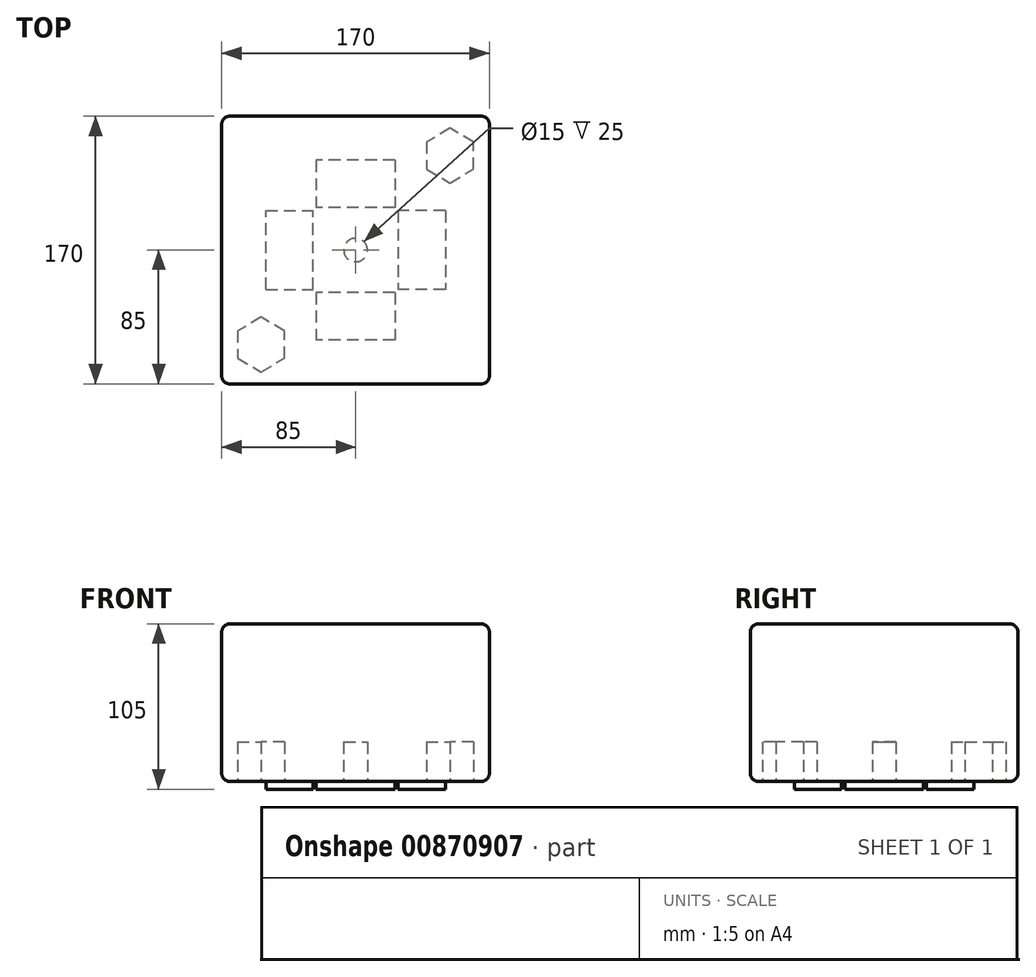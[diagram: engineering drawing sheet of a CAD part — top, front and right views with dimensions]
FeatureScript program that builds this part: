
annotation { "Feature Type Name" : "Feature", "Feature Type Description" : "" }
export const myFeature = defineFeature(function(context is Context, id is Id, definition is map)
    precondition{}
    {
        {
            var Q0;
            Q0=qCreatedBy(makeId("Top.planeOp"),FACE);
            var sketch = newSketch(context, id + "F0", { "sketchPlane" : qUnion([Q0])});
            skLineSegment(sketch, "E0.bottom", {"start": v(-85, 85) * mm, "end": v(85, 85) * mm});
            skLineSegment(sketch, "E0.top", {"start": v(-85, -85) * mm, "end": v(85, -85) * mm});
            skLineSegment(sketch, "E0.left", {"start": v(-85, 85) * mm, "end": v(-85, -85) * mm});
            skLineSegment(sketch, "E0.right", {"start": v(85, 85) * mm, "end": v(85, -85) * mm});
            skPoint(sketch, "E0.middle", {"position": v(0, 0) * mm});
            skSolve(sketch);
        }
        {
            var Q0;
            Q0=makeQuery(id+"F0.imprint","IMPRINT",FACE,{"disambiguationData":[TD([[makeQuery(id+"F0.imprint","IMPRINT",EDGE,{"derivedFrom":sQuery(id+"F0.wireOp",EDGE,"E0.bottom")}),-1.0]])]});
            extrude(context, id + "F1", {"entities" : qUnion([Q0]), "depth" : 100 * mm, "offsetDistance" : 25 * mm});
        }
        {
            var Q0;
            Q0=makeQuery(id+"F1.opExtrude","CAP_FACE",FACE,{"disambiguationData":[OSD([sQuery(id+"F0.wireOp",EDGE,"E0.bottom"),sQuery(id+"F0.wireOp",EDGE,"E0.top"),sQuery(id+"F0.wireOp",EDGE,"E0.left"),sQuery(id+"F0.wireOp",EDGE,"E0.right")])],"isStart":true});
            var sketch = newSketch(context, id + "F2", { "sketchPlane" : qUnion([Q0])});
            skCircle(sketch, "E1", {"center": v(0, 0) * mm, "radius": 7.5 * mm});
            skCircle(sketch, "E2.cCircle", {"center": v(-60, 60) * mm, "radius": 15 * mm, "construction": true});
            skLineSegment(sketch, "E2.0", {"start": v(-75, 68.66) * mm, "end": v(-60, 77.32) * mm});
            skLineSegment(sketch, "E2.1", {"start": v(-60, 77.32) * mm, "end": v(-45, 68.66) * mm});
            skLineSegment(sketch, "E2.2", {"start": v(-45, 68.66) * mm, "end": v(-45, 51.34) * mm});
            skLineSegment(sketch, "E2.3", {"start": v(-45, 51.34) * mm, "end": v(-60, 42.68) * mm});
            skLineSegment(sketch, "E2.4", {"start": v(-60, 42.68) * mm, "end": v(-75, 51.34) * mm});
            skLineSegment(sketch, "E2.5", {"start": v(-75, 51.34) * mm, "end": v(-75, 68.66) * mm});
            skPoint(sketch, "E2.0.midPoint", {"position": v(-67.5, 73) * mm});
            skCircle(sketch, "E3.cCircle", {"center": v(60, -60) * mm, "radius": 15 * mm, "construction": true});
            skLineSegment(sketch, "E3.0", {"start": v(75, -68.66) * mm, "end": v(60, -77.32) * mm});
            skLineSegment(sketch, "E3.1", {"start": v(60, -77.32) * mm, "end": v(45, -68.66) * mm});
            skLineSegment(sketch, "E3.2", {"start": v(45, -68.66) * mm, "end": v(45, -51.34) * mm});
            skLineSegment(sketch, "E3.3", {"start": v(45, -51.34) * mm, "end": v(60, -42.68) * mm});
            skLineSegment(sketch, "E3.4", {"start": v(60, -42.68) * mm, "end": v(75, -51.34) * mm});
            skLineSegment(sketch, "E3.5", {"start": v(75, -51.34) * mm, "end": v(75, -68.66) * mm});
            skPoint(sketch, "E3.0.midPoint", {"position": v(67.5, -73) * mm});
            skLineSegment(sketch, "E4", {"start": v(-60, 60) * mm, "end": v(-85, 60) * mm, "construction": true});
            skLineSegment(sketch, "E5", {"start": v(-60, 60) * mm, "end": v(-60, 85) * mm, "construction": true});
            skLineSegment(sketch, "E6", {"start": v(60, -60) * mm, "end": v(85, -60) * mm, "construction": true});
            skLineSegment(sketch, "E7", {"start": v(60, -60) * mm, "end": v(60, -85) * mm, "construction": true});
            skSolve(sketch);
        }
        {
            var Q0;
            Q0 = qSketchRegion(id + "F2", true);
            extrude(context, id + "F3", {"entities" : qUnion([Q0]), "operationType" : NewBodyOperationType.REMOVE, "oppositeDirection" : true, "depth" : 25 * mm, "offsetDistance" : 25 * mm});
        }
        {
            var Q0;
            Q0=makeQuery(id+"F1.opExtrude","SWEPT_EDGE",EDGE,{"disambiguationData":[OSD([sQuery(id+"F0.wireOp",EDGE,"E0.top"),sQuery(id+"F0.wireOp",EDGE,"E0.left")])]});
            var Q1;
            Q1=makeQuery(id+"F1.opExtrude","SWEPT_EDGE",EDGE,{"disambiguationData":[OSD([sQuery(id+"F0.wireOp",EDGE,"E0.top"),sQuery(id+"F0.wireOp",EDGE,"E0.right")])]});
            var Q2;
            Q2=makeQuery(id+"F1.opExtrude","SWEPT_EDGE",EDGE,{"disambiguationData":[OSD([sQuery(id+"F0.wireOp",EDGE,"E0.bottom"),sQuery(id+"F0.wireOp",EDGE,"E0.right")])]});
            var Q3;
            Q3=makeQuery(id+"F1.opExtrude","SWEPT_EDGE",EDGE,{"disambiguationData":[OSD([sQuery(id+"F0.wireOp",EDGE,"E0.bottom"),sQuery(id+"F0.wireOp",EDGE,"E0.left")])]});
            fillet(context, id + "F4", {"entities" : qUnion([Q0, Q1, Q2, Q3]), "radius" : 5 * mm, "tangentPropagation" : true, "allowEdgeOverflow" : false});
        }
        {
            var Q0;
            Q0=makeQuery(id+"F1.opExtrude","CAP_EDGE",EDGE,{"disambiguationData":[OSD([sQuery(id+"F0.wireOp",EDGE,"E0.top")])],"isStart":false});
            var Q1;
            Q1=makeQuery(id+"F1.opExtrude","CAP_EDGE",EDGE,{"disambiguationData":[OSD([sQuery(id+"F0.wireOp",EDGE,"E0.right")])],"isStart":true});
            fillet(context, id + "F5", {"entities" : qUnion([Q0, Q1]), "radius" : 5 * mm, "tangentPropagation" : true, "allowEdgeOverflow" : false});
        }
        {
            var Q0;
            Q0=makeQuery(id+"F1.opExtrude","CAP_FACE",FACE,{"disambiguationData":[OSD([sQuery(id+"F0.wireOp",EDGE,"E0.bottom"),sQuery(id+"F0.wireOp",EDGE,"E0.top"),sQuery(id+"F0.wireOp",EDGE,"E0.left"),sQuery(id+"F0.wireOp",EDGE,"E0.right")])],"isStart":true});
            var sketch = newSketch(context, id + "F6", { "sketchPlane" : qUnion([Q0])});
            skLineSegment(sketch, "E8", {"start": v(0, 0) * mm, "end": v(0, 42) * mm, "construction": true});
            skLineSegment(sketch, "E9.bottom", {"start": v(25, 27) * mm, "end": v(-25, 27) * mm});
            skLineSegment(sketch, "E9.top", {"start": v(25, 57) * mm, "end": v(-25, 57) * mm});
            skLineSegment(sketch, "E9.left", {"start": v(25, 27) * mm, "end": v(25, 57) * mm});
            skLineSegment(sketch, "E9.right", {"start": v(-25, 27) * mm, "end": v(-25, 57) * mm});
            skPoint(sketch, "E9.middle", {"position": v(0, 42) * mm});
            skLineSegment(sketch, "E10", {"start": v(0, 0) * mm, "end": v(42, 0) * mm, "construction": true});
            skLineSegment(sketch, "E11.bottom", {"start": v(57, -25) * mm, "end": v(27, -25) * mm});
            skLineSegment(sketch, "E11.top", {"start": v(57, 25) * mm, "end": v(27, 25) * mm});
            skLineSegment(sketch, "E11.left", {"start": v(57, -25) * mm, "end": v(57, 25) * mm});
            skLineSegment(sketch, "E11.right", {"start": v(27, -25) * mm, "end": v(27, 25) * mm});
            skPoint(sketch, "E11.middle", {"position": v(42, 0) * mm});
            skLineSegment(sketch, "E12", {"start": v(0, 0) * mm, "end": v(-42, 0) * mm, "construction": true});
            skLineSegment(sketch, "E13", {"start": v(0, 0) * mm, "end": v(0, -42) * mm, "construction": true});
            skPoint(sketch, "E14.middle", {"position": v(-42, 0) * mm});
            skPoint(sketch, "E15.middle", {"position": v(0, -42) * mm});
            skLineSegment(sketch, "E16.bottom", {"start": v(-57, 25) * mm, "end": v(-27, 25) * mm});
            skLineSegment(sketch, "E16.top", {"start": v(-57, -25) * mm, "end": v(-27, -25) * mm});
            skLineSegment(sketch, "E16.left", {"start": v(-57, 25) * mm, "end": v(-57, -25) * mm});
            skLineSegment(sketch, "E16.right", {"start": v(-27, 25) * mm, "end": v(-27, -25) * mm});
            skLineSegment(sketch, "E17.bottom", {"start": v(25, -57) * mm, "end": v(-25, -57) * mm});
            skLineSegment(sketch, "E17.top", {"start": v(25, -27) * mm, "end": v(-25, -27) * mm});
            skLineSegment(sketch, "E17.left", {"start": v(25, -57) * mm, "end": v(25, -27) * mm});
            skLineSegment(sketch, "E17.right", {"start": v(-25, -57) * mm, "end": v(-25, -27) * mm});
            skSolve(sketch);
        }
        {
            var Q0;
            Q0 = qSketchRegion(id + "F6", true);
            extrude(context, id + "F7", {"entities" : qUnion([Q0]), "operationType" : NewBodyOperationType.ADD, "depth" : 5 * mm, "offsetDistance" : 25 * mm});
        }
    });
